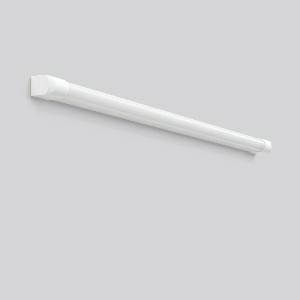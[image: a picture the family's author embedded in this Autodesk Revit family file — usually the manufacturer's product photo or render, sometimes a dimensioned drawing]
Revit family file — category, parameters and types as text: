
# Revit family: hb_507_451223_002_dc58
name_source: partatom
category: Lighting Fixtures
units: mm (PartAtom-declared; Revit-internal decimal feet)

## family parameters
Cut with Voids When Loaded = No
Host = Face
Light Source = No
Part Type = Normal
Room Calculation Point = No
Round Connector Dimension = Use Diameter
Shared = No

## types (1)
- MultiLumen 1 840 (1 x LED Modul 840, 1400 lm, 4000)
    Apparent Load = 11 VA
    CIE Flux Codes = 37 65 86 83 100
    Color Rendering = 80
    Color Temperature = 4000
    Default Elevation = 1800 mm
    Description = Series: HB 507
Linear luminaire, can be used as wall and mirror luminaire. Body and end caps made of white plastic. Diffuser: plastic, opal. Homogeneous and smooth light distribution. MultiColour: Colour temperature adjustable via switching element for 3000 K and 4000 K (factory setting). Suitable for Ceiling mounting, Wall (surface). Can be installed horizontally and vertically. Easy to install with stainless steel quick fastening clips. Converter integrated and encapsulated. 
Colour: white
Length: 1200 mm
Width: 42 mm
Height: 55 mm
Lamp: LED
Socket: without socket
Colour temperature: 3000K, 4000K
Colour rendering index (CRI): 80
System power: 11 W
Rated luminous flux: 1400 lm
Luminous efficiency: 127 lm/W
System power 2: 11 W
Rated luminous flux 2: 1300 lm
Luminous efficiency 2: 118 lm/W
Control gear: Regulated power supply
Protection class: II
Type of protection: IP 40
    Height = 55 mm
    Lamp = 1 x LED Modul 840
    Lamp Light Flux = 1400 lm
    Lamp count = 1
    Length = 1200 mm
    Lifetime = 50000 h
    Luminous efficacy = 127 lm/W
    Manufacturer = RZB
    ModVariant = No
    Model = 451223.002
    Mounting Place = Ceiling
    Mounting Type = Surface mounted
    Number of Poles = 1
    OnlyDefault = Yes
    Power Factor = 1
    Product Name = HB 507
    Product group = Surface mounted ceiling and wall luminaires
    ProductGroupID = 305
    Protection Class = Protection class II
    Protection Degree = Degree of protection
    RLX_Detail_Level = 1
    RLX_Emergency_Light_Flux = 0 lm
    RLX_Emergency_Type = 0
    RLX_Emergency_Type_DB = No
    RlxData = <blob elided: 40461 chars, md5=21ee0cab>
    Socket = socket
    Standby Power = 0 W
    System Light Flux = 1400 lm
    System Power = 11 W
    Type Comments = MultiLumen 1 840
    Type Image = 451223.002.jpg
    URL = http://relux.com
    VarID = multilumen_1_840
    Voltage = 0 V
    Weight = 0.00 kg
    Width = 42 mm

## geometry (parser evidence)
native form markers: Blend x4, Sweep x12
no freeform markers — native parametric forms only
